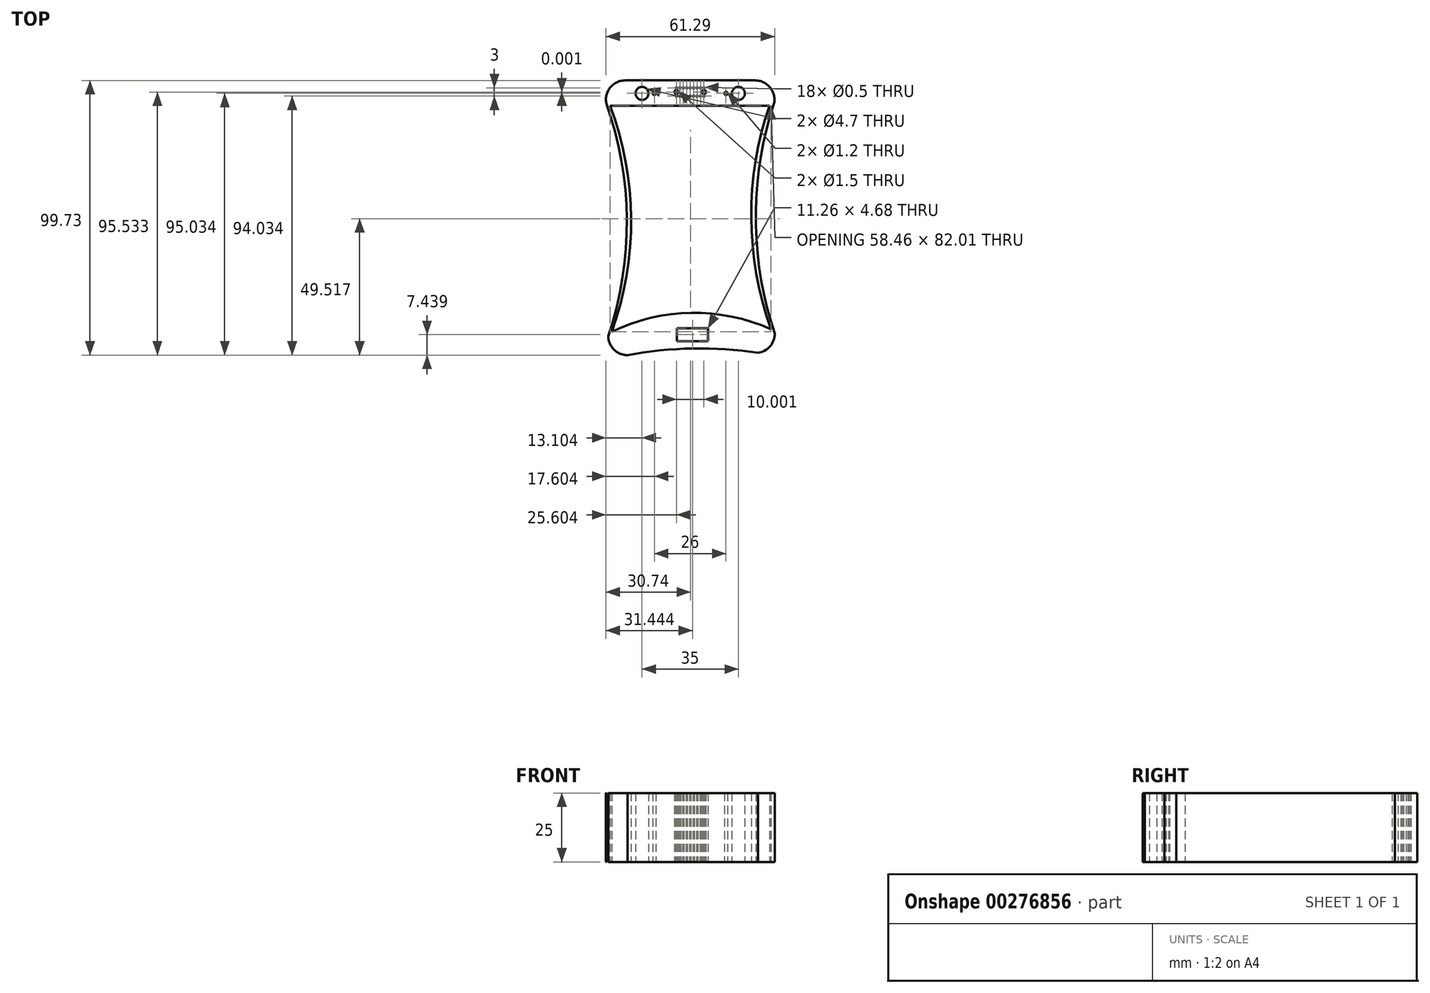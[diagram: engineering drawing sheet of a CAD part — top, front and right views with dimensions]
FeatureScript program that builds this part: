
annotation { "Feature Type Name" : "Feature", "Feature Type Description" : "" }
export const myFeature = defineFeature(function(context is Context, id is Id, definition is map)
    precondition{}
    {
        {
            var Q0;
            Q0=qCreatedBy(makeId("Top.planeOp"),FACE);
            var sketch = newSketch(context, id + "F0", { "sketchPlane" : qUnion([Q0])});
            skLineSegment(sketch, "E0", {"start": v(-32.8, 29.74) * mm, "end": v(14.4, 29.74) * mm});
            skPoint(sketch, "E1.visualSharp", {"position": v(21.51, 29.74) * mm});
            skArc(sketch, "E1.filletArc", {"start": v(21.3, 21.54) * mm, "mid": v(19.76, 27.25) * mm, "end": v(14.4, 29.74) * mm});
            skPoint(sketch, "E2.visualSharp", {"position": v(21.51, -70.26) * mm});
            skArc(sketch, "E2.filletArc", {"start": v(15.45, -69.17) * mm, "mid": v(19.8, -66.78) * mm, "end": v(21.48, -62.1) * mm});
            skPoint(sketch, "E3.visualSharp", {"position": v(-38.49, -70.26) * mm});
            skArc(sketch, "E3.filletArc", {"start": v(-38.96, -63) * mm, "mid": v(-36.9, -67.94) * mm, "end": v(-31.96, -70) * mm});
            skPoint(sketch, "E4.visualSharp", {"position": v(-38.49, 29.74) * mm});
            skArc(sketch, "E4.filletArc", {"start": v(-32.8, 29.74) * mm, "mid": v(-38.17, 27.25) * mm, "end": v(-39.7, 21.54) * mm});
            skArc(sketch, "E5", {"start": v(21.3, 21.54) * mm, "mid": v(14.61, -20.3) * mm, "end": v(21.48, -62.1) * mm});
            skPoint(sketch, "E5.third.point", {"position": v(18.87, 13.32) * mm});
            skArc(sketch, "E6", {"start": v(-38.96, -63) * mm, "mid": v(-32.22, -20.66) * mm, "end": v(-39.7, 21.54) * mm});
            skPoint(sketch, "E6.third.point", {"position": v(-33.81, -42.06) * mm});
            skLineSegment(sketch, "E7", {"start": v(-39.7, 21.54) * mm, "end": v(21.3, 21.54) * mm});
            skArc(sketch, "E8", {"start": v(15.45, -69.17) * mm, "mid": v(-8.29, -67.58) * mm, "end": v(-31.96, -70) * mm});
            skPoint(sketch, "E8.third.point", {"position": v(-2.6, -67.6) * mm});
            skArc(sketch, "E9", {"start": v(21.48, -62.1) * mm, "mid": v(-8.84, -55.72) * mm, "end": v(-38.96, -63) * mm});
            skPoint(sketch, "E9.third.point", {"position": v(-9.51, -55.73) * mm});
            skPoint(sketch, "E10.end.orphan", {"position": v(-14.01, -55.99) * mm});
            skPoint(sketch, "E11.end.orphan", {"position": v(-2.81, -55.99) * mm});
            skCircle(sketch, "E12", {"center": v(-26.7, 25.04) * mm, "radius": 2.35 * mm});
            skCircle(sketch, "E13", {"center": v(8.3, 25.04) * mm, "radius": 2.35 * mm});
            skCircle(sketch, "E14", {"center": v(-22.2, 25.04) * mm, "radius": 0.6 * mm});
            skCircle(sketch, "E15", {"center": v(3.8, 25.04) * mm, "radius": 0.6 * mm});
            skPoint(sketch, "E16.startSnap0", {"position": v(-8.84, -55.72) * mm});
            skPoint(sketch, "E16.start.orphan", {"position": v(-8.84, -55.72) * mm});
            skLineSegment(sketch, "E17", {"start": v(-14, -60.21) * mm, "end": v(-2.74, -60.21) * mm});
            skPoint(sketch, "E18.end.orphan", {"position": v(-2.77, -63.14) * mm});
            skPoint(sketch, "E19.start.orphan", {"position": v(-13.97, -63.14) * mm});
            skLineSegment(sketch, "E20", {"start": v(-2.74, -60.21) * mm, "end": v(-2.74, -64.9) * mm});
            skLineSegment(sketch, "E21", {"start": v(-2.74, -64.9) * mm, "end": v(-14, -64.9) * mm});
            skLineSegment(sketch, "E22", {"start": v(-14, -64.9) * mm, "end": v(-14, -60.21) * mm});
            skLineSegment(sketch, "E23", {"start": v(-38.3, 20.53) * mm, "end": v(19.57, 20.53) * mm});
            skLineSegment(sketch, "E24", {"start": v(-31.96, -70) * mm, "end": v(-34.96, -70) * mm});
            skLineSegment(sketch, "E25", {"start": v(20.1, -57.76) * mm, "end": v(21.48, -62.1) * mm});
            skLineSegment(sketch, "E26", {"start": v(20.7, -59.65) * mm, "end": v(20.68, -59.64) * mm});
            skArc(sketch, "E27", {"start": v(20.16, -60.6) * mm, "mid": v(-8.84, -54.64) * mm, "end": v(-37.65, -61.48) * mm});
            skPoint(sketch, "E28.endSnap0", {"position": v(-8.84, -54.64) * mm});
            skPoint(sketch, "E29.end.orphan", {"position": v(-34.96, -61.17) * mm});
            skPoint(sketch, "E30.end.orphan", {"position": v(19.34, -61.17) * mm});
            skPoint(sketch, "E28.end.orphan", {"position": v(-8.85, -54.64) * mm});
            skLineSegment(sketch, "E31", {"start": v(-8.85, -54.64) * mm, "end": v(-8.84, -55.72) * mm});
            skArc(sketch, "E32", {"start": v(-37.65, -61.48) * mm, "mid": v(-30.67, -20.42) * mm, "end": v(-38.3, 20.53) * mm});
            skArc(sketch, "E33", {"start": v(19.57, 20.53) * mm, "mid": v(12.96, -20.08) * mm, "end": v(20.16, -60.6) * mm});
            skLineSegment(sketch, "E34", {"start": v(-22.2, 25.04) * mm, "end": v(-21.6, 25.04) * mm});
            skLineSegment(sketch, "E35", {"start": v(3.8, 25.04) * mm, "end": v(3.2, 25.04) * mm});
            skLineSegment(sketch, "E36", {"start": v(-14.2, 27.04) * mm, "end": v(-14.2, 27.04) * mm});
            skLineSegment(sketch, "E37", {"start": v(-14.2, 24.04) * mm, "end": v(-13.96, 24.04) * mm});
            skLineSegment(sketch, "E38", {"start": v(-14.2, 27.04) * mm, "end": v(-14.2, 26.8) * mm});
            skLineSegment(sketch, "E39", {"start": v(-4.2, 24.04) * mm, "end": v(-4.2, 24.3) * mm});
            skLineSegment(sketch, "E40", {"start": v(-14.2, 27.04) * mm, "end": v(-13.96, 27.04) * mm});
            skCircle(sketch, "E41", {"center": v(-14.2, 27.04) * mm, "radius": 0.25 * mm});
            skCircle(sketch, "E42", {"center": v(-14.2, 24.04) * mm, "radius": 0.25 * mm});
            skCircle(sketch, "E43", {"center": v(-4.2, 24.04) * mm, "radius": 0.25 * mm});
            skCircle(sketch, "E44", {"center": v(-4.2, 27.04) * mm, "radius": 0.25 * mm});
            skCircle(sketch, "E45", {"center": v(-9.2, 27.04) * mm, "radius": 0.25 * mm});
            skCircle(sketch, "E46", {"center": v(-9.2, 24.04) * mm, "radius": 0.25 * mm});
            skCircle(sketch, "E47", {"center": v(-11.7, 27.04) * mm, "radius": 0.25 * mm});
            skCircle(sketch, "E48", {"center": v(-11.7, 24.04) * mm, "radius": 0.25 * mm});
            skCircle(sketch, "E49", {"center": v(-6.7, 24.04) * mm, "radius": 0.25 * mm});
            skCircle(sketch, "E50", {"center": v(-6.7, 27.04) * mm, "radius": 0.25 * mm});
            skCircle(sketch, "E51", {"center": v(-12.96, 27.04) * mm, "radius": 0.25 * mm});
            skCircle(sketch, "E52", {"center": v(-12.96, 24.04) * mm, "radius": 0.25 * mm});
            skCircle(sketch, "E53", {"center": v(-7.96, 27.04) * mm, "radius": 0.25 * mm});
            skCircle(sketch, "E54", {"center": v(-7.96, 24.04) * mm, "radius": 0.25 * mm});
            skCircle(sketch, "E55", {"center": v(-5.46, 27.04) * mm, "radius": 0.25 * mm});
            skCircle(sketch, "E56", {"center": v(-5.46, 24.04) * mm, "radius": 0.25 * mm});
            skCircle(sketch, "E57", {"center": v(-10.46, 27.04) * mm, "radius": 0.25 * mm});
            skCircle(sketch, "E58", {"center": v(-10.46, 24.04) * mm, "radius": 0.25 * mm});
            skCircle(sketch, "E59", {"center": v(-14.2, 25.54) * mm, "radius": 0.75 * mm});
            skCircle(sketch, "E60", {"center": v(-4.2, 25.54) * mm, "radius": 0.75 * mm});
            skLineSegment(sketch, "E61.trimOffspring", {"start": v(-14.2, 26.3) * mm, "end": v(-14.2, 24.04) * mm});
            skLineSegment(sketch, "E62.trimOffspring", {"start": v(-13.2, 27.04) * mm, "end": v(-12.7, 27.04) * mm});
            skLineSegment(sketch, "E63.trimOffspring", {"start": v(-11.96, 27.04) * mm, "end": v(-11.7, 27.04) * mm});
            skLineSegment(sketch, "E64.trimOffspring", {"start": v(-10.7, 27.04) * mm, "end": v(-10.2, 27.04) * mm});
            skLineSegment(sketch, "E65.trimOffspring", {"start": v(-8.2, 27.04) * mm, "end": v(-7.7, 27.04) * mm});
            skLineSegment(sketch, "E66.trimOffspring", {"start": v(-6.96, 27.04) * mm, "end": v(-6.46, 27.04) * mm});
            skLineSegment(sketch, "E67.trimOffspring", {"start": v(-5.7, 27.04) * mm, "end": v(-5.2, 27.04) * mm});
            skLineSegment(sketch, "E68.trimOffspring", {"start": v(-9.46, 27.04) * mm, "end": v(-8.96, 27.04) * mm});
            skLineSegment(sketch, "E69.trimOffspring", {"start": v(-4.46, 27.04) * mm, "end": v(-4.2, 27.04) * mm});
            skLineSegment(sketch, "E70.trimOffspring", {"start": v(-4.2, 26.8) * mm, "end": v(-4.2, 27.04) * mm});
            skLineSegment(sketch, "E71.trimOffspring", {"start": v(-4.2, 24.8) * mm, "end": v(-4.2, 26.3) * mm});
            skLineSegment(sketch, "E72.trimOffspring", {"start": v(-4.46, 24.04) * mm, "end": v(-4.2, 24.04) * mm});
            skLineSegment(sketch, "E73.trimOffspring", {"start": v(-5.7, 24.04) * mm, "end": v(-5.46, 24.04) * mm});
            skLineSegment(sketch, "E74.trimOffspring", {"start": v(-6.96, 24.04) * mm, "end": v(-6.46, 24.04) * mm});
            skLineSegment(sketch, "E75.trimOffspring", {"start": v(-8.2, 24.04) * mm, "end": v(-7.7, 24.04) * mm});
            skLineSegment(sketch, "E76.trimOffspring", {"start": v(-10.7, 24.04) * mm, "end": v(-10.2, 24.04) * mm});
            skLineSegment(sketch, "E77.trimOffspring", {"start": v(-9.46, 24.04) * mm, "end": v(-8.96, 24.04) * mm});
            skLineSegment(sketch, "E78.trimOffspring", {"start": v(-11.96, 24.04) * mm, "end": v(-11.46, 24.04) * mm});
            skLineSegment(sketch, "E79.trimOffspring", {"start": v(-13.2, 24.04) * mm, "end": v(-12.7, 24.04) * mm});
            skPoint(sketch, "E80.start.orphan", {"position": v(-30.67, -20.42) * mm});
            skSolve(sketch);
        }
        {
            var Q0;
            Q0 = qSketchRegion(id + "F0", true);
            extrude(context, id + "F1", {"entities" : qUnion([Q0]), "depth" : 25 * mm});
        }
    });
